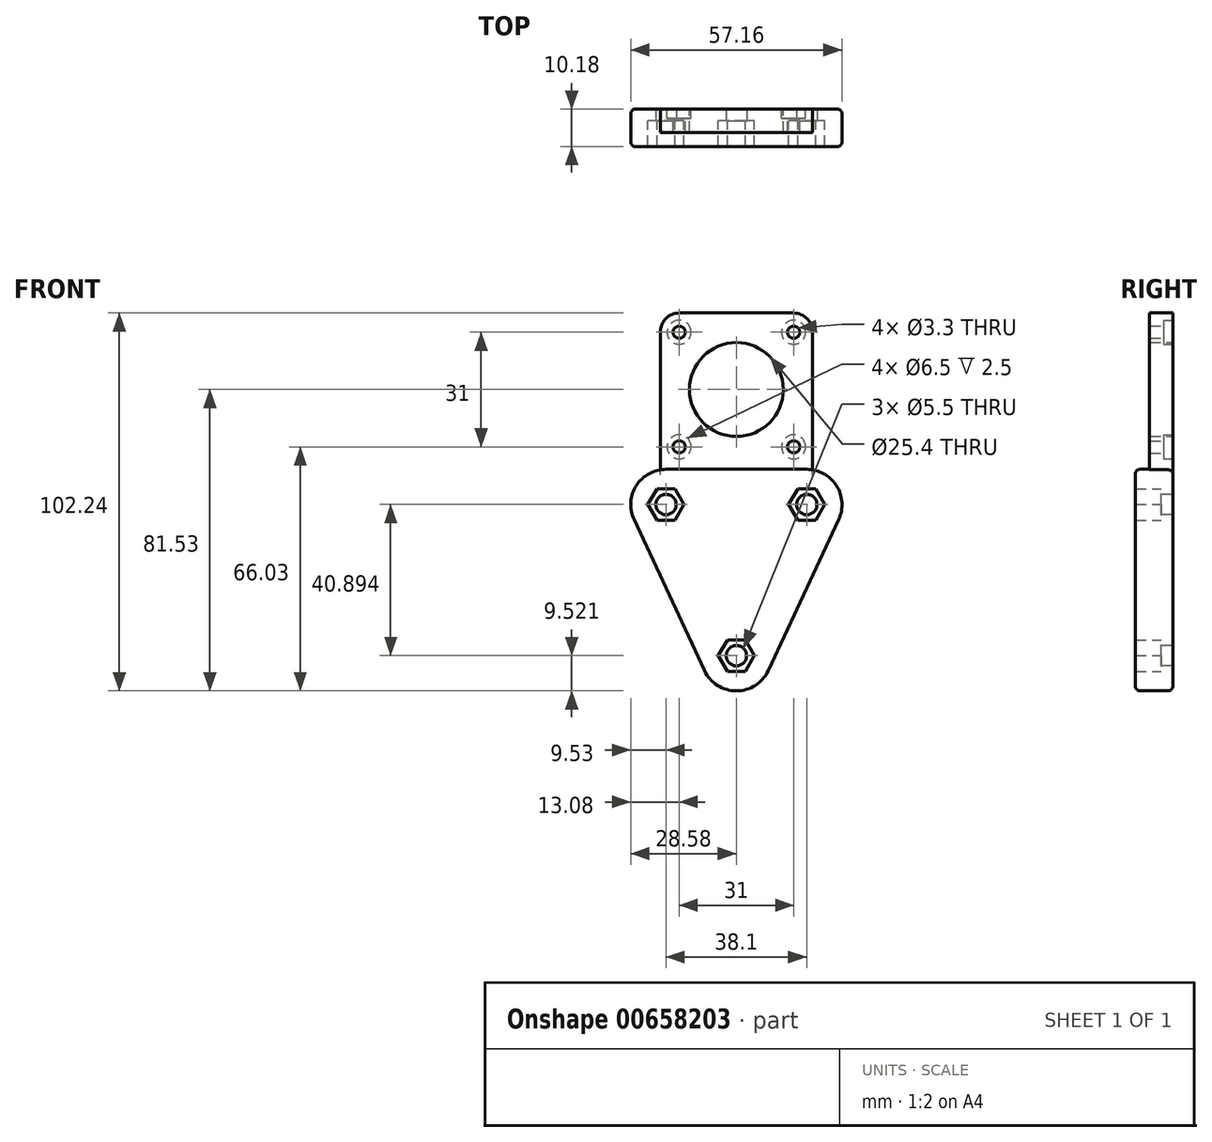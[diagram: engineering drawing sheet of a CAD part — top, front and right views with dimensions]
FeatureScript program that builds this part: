
annotation { "Feature Type Name" : "Feature", "Feature Type Description" : "" }
export const myFeature = defineFeature(function(context is Context, id is Id, definition is map)
    precondition{}
    {
        {
            var Q0;
            Q0=qCreatedBy(makeId("Front.planeOp"),FACE);
            var sketch = newSketch(context, id + "F0", { "sketchPlane" : qUnion([Q0])});
            skLineSegment(sketch, "E0", {"start": v(0, -50.42) * mm, "end": v(0, 37.12) * mm, "construction": true});
            skCircle(sketch, "E1", {"center": v(-19.05, -9.53) * mm, "radius": 2.75 * mm});
            skCircle(sketch, "E2", {"center": v(0, -50.42) * mm, "radius": 2.75 * mm});
            skCircle(sketch, "E3", {"center": v(19.05, -9.53) * mm, "radius": 2.75 * mm});
            skArc(sketch, "E4", {"start": v(-19.05, 0) * mm, "mid": v(-27.08, -4.4) * mm, "end": v(-27.68, -13.55) * mm});
            skArc(sketch, "E5", {"start": v(27.68, -13.55) * mm, "mid": v(27.08, -4.4) * mm, "end": v(19.05, 0) * mm});
            skArc(sketch, "E6", {"start": v(-8.63, -54.44) * mm, "mid": v(0, -59.94) * mm, "end": v(8.63, -54.44) * mm});
            skLineSegment(sketch, "E7", {"start": v(-19.05, 0) * mm, "end": v(19.05, 0) * mm});
            skLineSegment(sketch, "E8", {"start": v(8.63, -54.44) * mm, "end": v(27.68, -13.55) * mm});
            skLineSegment(sketch, "E9.MirrorCS", {"start": v(-8.63, -54.44) * mm, "end": v(-27.68, -13.55) * mm});
            skPoint(sketch, "E10", {"position": v(0, 0) * mm});
            skCircle(sketch, "E11.cCircle", {"center": v(-19.05, -9.53) * mm, "radius": 4.25 * mm, "construction": true});
            skLineSegment(sketch, "E11.0", {"start": v(-16.6, -13.78) * mm, "end": v(-21.5, -13.78) * mm});
            skLineSegment(sketch, "E11.1", {"start": v(-21.5, -13.78) * mm, "end": v(-23.96, -9.53) * mm});
            skLineSegment(sketch, "E11.2", {"start": v(-23.96, -9.53) * mm, "end": v(-21.5, -5.27) * mm});
            skLineSegment(sketch, "E11.3", {"start": v(-21.5, -5.28) * mm, "end": v(-16.6, -5.28) * mm});
            skLineSegment(sketch, "E11.4", {"start": v(-16.6, -5.27) * mm, "end": v(-14.14, -9.52) * mm});
            skLineSegment(sketch, "E11.5", {"start": v(-14.14, -9.52) * mm, "end": v(-16.6, -13.78) * mm});
            skPoint(sketch, "E11.0.midPoint", {"position": v(-19.05, -13.78) * mm});
            skCircle(sketch, "E12.cCircle", {"center": v(19.05, -9.53) * mm, "radius": 4.25 * mm, "construction": true});
            skLineSegment(sketch, "E12.0", {"start": v(21.5, -13.78) * mm, "end": v(16.6, -13.78) * mm});
            skLineSegment(sketch, "E12.1", {"start": v(16.6, -13.78) * mm, "end": v(14.14, -9.52) * mm});
            skLineSegment(sketch, "E12.2", {"start": v(14.14, -9.52) * mm, "end": v(16.6, -5.27) * mm});
            skLineSegment(sketch, "E12.3", {"start": v(16.6, -5.27) * mm, "end": v(21.5, -5.27) * mm});
            skLineSegment(sketch, "E12.4", {"start": v(21.5, -5.27) * mm, "end": v(23.96, -9.53) * mm});
            skLineSegment(sketch, "E12.5", {"start": v(23.96, -9.53) * mm, "end": v(21.5, -13.78) * mm});
            skPoint(sketch, "E12.0.midPoint", {"position": v(19.05, -13.78) * mm});
            skCircle(sketch, "E13.cCircle", {"center": v(0, -50.42) * mm, "radius": 4.25 * mm, "construction": true});
            skLineSegment(sketch, "E13.0", {"start": v(2.45, -54.67) * mm, "end": v(-2.45, -54.67) * mm});
            skLineSegment(sketch, "E13.1", {"start": v(-2.45, -54.67) * mm, "end": v(-4.9, -50.42) * mm});
            skLineSegment(sketch, "E13.2", {"start": v(-4.9, -50.42) * mm, "end": v(-2.45, -46.17) * mm});
            skLineSegment(sketch, "E13.3", {"start": v(-2.45, -46.17) * mm, "end": v(2.45, -46.17) * mm});
            skLineSegment(sketch, "E13.4", {"start": v(2.45, -46.17) * mm, "end": v(4.9, -50.42) * mm});
            skLineSegment(sketch, "E13.5", {"start": v(4.9, -50.42) * mm, "end": v(2.45, -54.67) * mm});
            skPoint(sketch, "E13.0.midPoint", {"position": v(0, -54.67) * mm});
            skSolve(sketch);
        }
        {
            var Q0;
            Q0=makeQuery(id+"F0.imprint","IMPRINT",FACE,{"disambiguationData":[TD([[makeQuery(id+"F0.imprint","IMPRINT",EDGE,{"derivedFrom":sQuery(id+"F0.wireOp",EDGE,"E4")}),1.0]])]});
            extrude(context, id + "F1", {"entities" : qUnion([Q0]), "depth" : 7 * mm, "offsetDistance" : 25.4 * mm});
        }
        {
            var Q0;
            Q0=makeQuery(id+"F0.imprint","IMPRINT",FACE,{"disambiguationData":[TD([[makeQuery(id+"F0.imprint","IMPRINT",EDGE,{"derivedFrom":sQuery(id+"F0.wireOp",EDGE,"E4")}),1.0]])]});
            var Q1;
            Q1=makeQuery(id+"F0.imprint","IMPRINT",FACE,{"disambiguationData":[TD([[makeQuery(id+"F0.imprint","IMPRINT",EDGE,{"derivedFrom":sQuery(id+"F0.wireOp",EDGE,"E3")}),-1.0]])]});
            var Q2;
            Q2=makeQuery(id+"F0.imprint","IMPRINT",FACE,{"disambiguationData":[TD([[makeQuery(id+"F0.imprint","IMPRINT",EDGE,{"derivedFrom":sQuery(id+"F0.wireOp",EDGE,"E1")}),-1.0]])]});
            var Q3;
            Q3=makeQuery(id+"F0.imprint","IMPRINT",FACE,{"disambiguationData":[TD([[makeQuery(id+"F0.imprint","IMPRINT",EDGE,{"derivedFrom":sQuery(id+"F0.wireOp",EDGE,"E2")}),-1.0]])]});
            extrude(context, id + "F2", {"entities" : qUnion([Q0, Q1, Q2, Q3]), "operationType" : NewBodyOperationType.ADD, "oppositeDirection" : true, "depth" : 3.17 * mm, "offsetDistance" : 25.4 * mm});
        }
        {
            var Q0;
            Q0=makeQuery(id+"F2.opExtrude","CAP_FACE",FACE,{"disambiguationData":[OSD([sQuery(id+"F0.wireOp",EDGE,"E1"),sQuery(id+"F0.wireOp",EDGE,"E2"),sQuery(id+"F0.wireOp",EDGE,"E3"),sQuery(id+"F0.wireOp",EDGE,"E4"),sQuery(id+"F0.wireOp",EDGE,"E5"),sQuery(id+"F0.wireOp",EDGE,"E6"),sQuery(id+"F0.wireOp",EDGE,"E7"),sQuery(id+"F0.wireOp",EDGE,"E8"),sQuery(id+"F0.wireOp",EDGE,"E9.MirrorCS")])],"isStart":false});
            var sketch = newSketch(context, id + "F3", { "sketchPlane" : qUnion([Q0])});
            skLineSegment(sketch, "E14.top", {"start": v(20.57, 42.3) * mm, "end": v(-20.57, 42.3) * mm});
            skLineSegment(sketch, "E14.left", {"start": v(20.57, -0.12) * mm, "end": v(20.57, 42.3) * mm});
            skLineSegment(sketch, "E14.right", {"start": v(-20.57, -0.12) * mm, "end": v(-20.57, 42.3) * mm});
            skCircle(sketch, "E15", {"center": v(0, 21.59) * mm, "radius": 12.7 * mm});
            skPoint(sketch, "E15.centerSnap0", {"position": v(0, 42.3) * mm});
            skPoint(sketch, "E15.centerSnap1", {"position": v(20.57, 21.59) * mm});
            skPoint(sketch, "E16", {"position": v(15.5, 37.09) * mm});
            skPoint(sketch, "E17.MirrorP", {"position": v(-15.5, 37.09) * mm});
            skLineSegment(sketch, "E18", {"start": v(0, 21.59) * mm, "end": v(6, 21.59) * mm, "construction": true});
            skPoint(sketch, "E19.MirrorP", {"position": v(15.5, 6.1) * mm});
            skPoint(sketch, "E20.MirrorP", {"position": v(-15.5, 6.1) * mm});
            skSolve(sketch);
        }
        {
            var Q0;
            Q0=makeQuery(id+"F3.imprint","IMPRINT",FACE,{"disambiguationData":[TD([[makeQuery(id+"F3.imprint","IMPRINT",EDGE,{"derivedFrom":sQuery(id+"F3.wireOp",EDGE,"E14.top")}),1.0]])]});
            extrude(context, id + "F4", {"entities" : qUnion([Q0]), "operationType" : NewBodyOperationType.ADD, "oppositeDirection" : true, "depth" : 6.35 * mm, "offsetDistance" : 25.4 * mm});
        }
        {
            var Q0;
            Q0=sQuery(id+"F3.wireOp",VERTEX,"E17.MirrorP");
            var Q1;
            Q1=sQuery(id+"F3.wireOp",VERTEX,"E16");
            var Q2;
            Q2=sQuery(id+"F3.wireOp",VERTEX,"E19.MirrorP");
            var Q3;
            Q3=sQuery(id+"F3.wireOp",VERTEX,"E20.MirrorP");
            var Q4;
            Q4=makeQuery(id+"F1.opExtrude","SWEPT_BODY",BODY,{"disambiguationData":[OSD([sQuery(id+"F0.wireOp",EDGE,"E4"),sQuery(id+"F0.wireOp",EDGE,"E5"),sQuery(id+"F0.wireOp",EDGE,"E6"),sQuery(id+"F0.wireOp",EDGE,"E7"),sQuery(id+"F0.wireOp",EDGE,"E8"),sQuery(id+"F0.wireOp",EDGE,"E9.MirrorCS"),sQuery(id+"F0.wireOp",EDGE,"E11.0"),sQuery(id+"F0.wireOp",EDGE,"E11.1"),sQuery(id+"F0.wireOp",EDGE,"E11.2"),sQuery(id+"F0.wireOp",EDGE,"E11.3"),sQuery(id+"F0.wireOp",EDGE,"E11.4"),sQuery(id+"F0.wireOp",EDGE,"E11.5"),sQuery(id+"F0.wireOp",EDGE,"E12.0"),sQuery(id+"F0.wireOp",EDGE,"E12.1"),sQuery(id+"F0.wireOp",EDGE,"E12.2"),sQuery(id+"F0.wireOp",EDGE,"E12.3"),sQuery(id+"F0.wireOp",EDGE,"E12.4"),sQuery(id+"F0.wireOp",EDGE,"E12.5"),sQuery(id+"F0.wireOp",EDGE,"E13.0"),sQuery(id+"F0.wireOp",EDGE,"E13.1"),sQuery(id+"F0.wireOp",EDGE,"E13.2"),sQuery(id+"F0.wireOp",EDGE,"E13.3"),sQuery(id+"F0.wireOp",EDGE,"E13.4"),sQuery(id+"F0.wireOp",EDGE,"E13.5")])]});
            hole(context, id + "F5", {"style" : HoleStyle.C_BORE, "endStyle" : HoleEndStyle.THROUGH, "holeDiameter" : 3.3 * mm, "cBoreDiameter" : 6.5 * mm, "cBoreDepth" : 2.5 * mm, "majorDiameter" : 6.35 * mm, "isTappedThrough" : true, "tappedDepth" : 12.7 * mm, "tapClearance" : 3, "locations" : qUnion([Q0, Q1, Q2, Q3]), "scope" : qUnion([Q4])});
        }
        {
            var Q0;
            Q0=makeQuery(id+"F4.opExtrude","SWEPT_EDGE",EDGE,{"disambiguationData":[OSD([sQuery(id+"F3.wireOp",EDGE,"E14.top"),sQuery(id+"F3.wireOp",EDGE,"E14.right")])]});
            var Q1;
            Q1=makeQuery(id+"F4.opExtrude","SWEPT_EDGE",EDGE,{"disambiguationData":[OSD([sQuery(id+"F3.wireOp",EDGE,"E14.top"),sQuery(id+"F3.wireOp",EDGE,"E14.left")])]});
            var Q2;
            Q2=makeQuery(id+"F4.opExtrude","SWEPT_EDGE",EDGE,{"disambiguationData":[OSD([sQuery(id+"F0.wireOp",EDGE,"E4"),sQuery(id+"F3.wireOp",EDGE,"E14.left")])]});
            var Q3;
            Q3=makeQuery(id+"F4.opExtrude","SWEPT_EDGE",EDGE,{"disambiguationData":[OSD([sQuery(id+"F0.wireOp",EDGE,"E5"),sQuery(id+"F3.wireOp",EDGE,"E14.right")])]});
            fillet(context, id + "F6", {"entities" : qUnion([Q0, Q1, Q2, Q3]), "radius" : 5.08 * mm, "tangentPropagation" : true, "allowEdgeOverflow" : false});
        }
        {
            var Q0;
            Q0=makeQuery(id+"F2.opExtrude","CAP_EDGE",EDGE,{"disambiguationData":[OSD([sQuery(id+"F0.wireOp",EDGE,"E5")])],"isStart":false});
            var Q1;
            Q1=makeQuery(id+"F1.opExtrude","CAP_EDGE",EDGE,{"disambiguationData":[OSD([sQuery(id+"F0.wireOp",EDGE,"E8")])],"isStart":false});
            fillet(context, id + "F7", {"entities" : qUnion([Q0, Q1]), "radius" : 1.27 * mm, "tangentPropagation" : true, "allowEdgeOverflow" : false});
        }
    });
